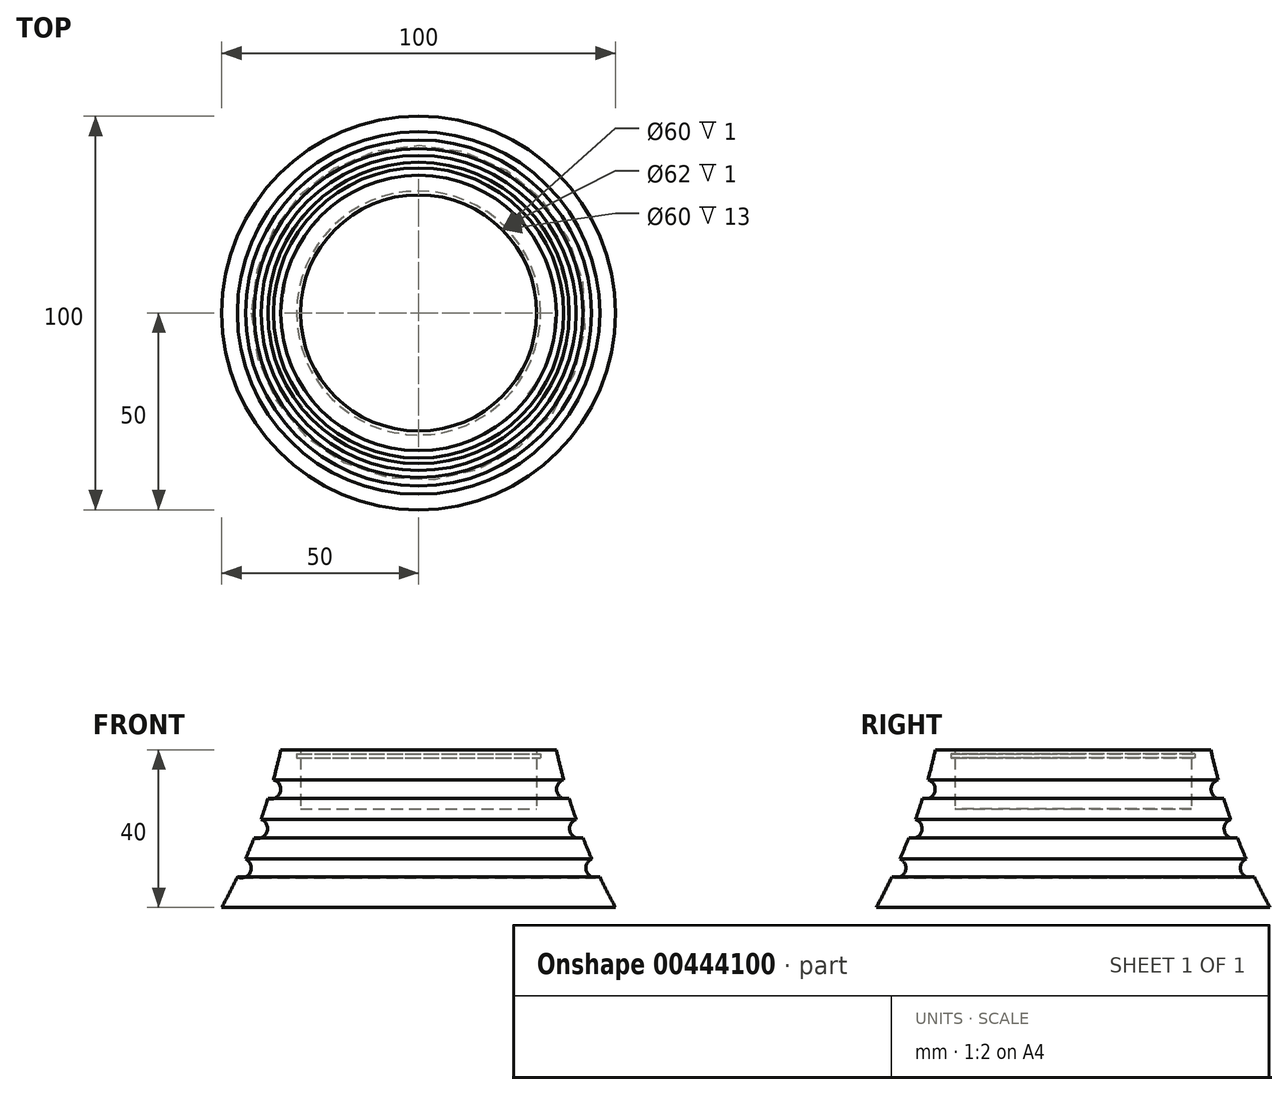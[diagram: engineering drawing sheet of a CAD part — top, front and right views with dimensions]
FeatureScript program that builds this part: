
annotation { "Feature Type Name" : "Feature", "Feature Type Description" : "" }
export const myFeature = defineFeature(function(context is Context, id is Id, definition is map)
    precondition{}
    {
        {
            var Q0;
            Q0=qCreatedBy(makeId("Front.planeOp"),FACE);
            var sketch = newSketch(context, id + "F0", { "sketchPlane" : qUnion([Q0])});
            skLineSegment(sketch, "E0", {"start": v(0, 0) * mm, "end": v(0, 25) * mm});
            skLineSegment(sketch, "E1", {"start": v(30, 25) * mm, "end": v(0, 25) * mm});
            skLineSegment(sketch, "E2", {"start": v(30, 40) * mm, "end": v(30, 39) * mm});
            skLineSegment(sketch, "E3", {"start": v(30, 40) * mm, "end": v(35, 40) * mm});
            skLineSegment(sketch, "E4", {"start": v(0, 0) * mm, "end": v(50, 0) * mm});
            skArc(sketch, "E5", {"start": v(35, 40) * mm, "mid": v(35.89, 36.2) * mm, "end": v(36.87, 32.4) * mm});
            skLineSegment(sketch, "E6.bottom", {"start": v(30, 39) * mm, "end": v(31, 39) * mm});
            skLineSegment(sketch, "E6.top", {"start": v(30, 38) * mm, "end": v(31, 38) * mm});
            skLineSegment(sketch, "E6.right", {"start": v(31, 39) * mm, "end": v(31, 38) * mm});
            skLineSegment(sketch, "E7.trimOffspring", {"start": v(30, 38) * mm, "end": v(30, 25) * mm});
            skArc(sketch, "E8", {"start": v(36.87, 32.4) * mm, "mid": v(35.16, 29.3) * mm, "end": v(38.28, 27.6) * mm});
            skArc(sketch, "E9", {"start": v(40.02, 22.35) * mm, "mid": v(38.52, 19.13) * mm, "end": v(41.76, 17.66) * mm});
            skArc(sketch, "E10", {"start": v(43.97, 12.28) * mm, "mid": v(42.72, 8.96) * mm, "end": v(46.05, 7.73) * mm});
            skArc(sketch, "E11.trimOffspring", {"start": v(38.28, 27.6) * mm, "mid": v(39.12, 24.97) * mm, "end": v(40.02, 22.35) * mm});
            skArc(sketch, "E12.trimOffspring", {"start": v(41.76, 17.66) * mm, "mid": v(42.84, 14.96) * mm, "end": v(43.97, 12.28) * mm});
            skArc(sketch, "E13.trimOffspring", {"start": v(46.05, 7.73) * mm, "mid": v(47.97, 3.84) * mm, "end": v(50, 0) * mm});
            skSolve(sketch);
        }
        {
            var Q0;
            Q0 = qSketchRegion(id + "F0", true);
            var Q1;
            Q1=sQuery(id+"F0.wireOp",EDGE,"E0");
            revolve(context, id + "F1", {"entities" : qUnion([Q0]), "axis" : qUnion([Q1]), "revolveType" : RevolveType.FULL});
        }
    });
